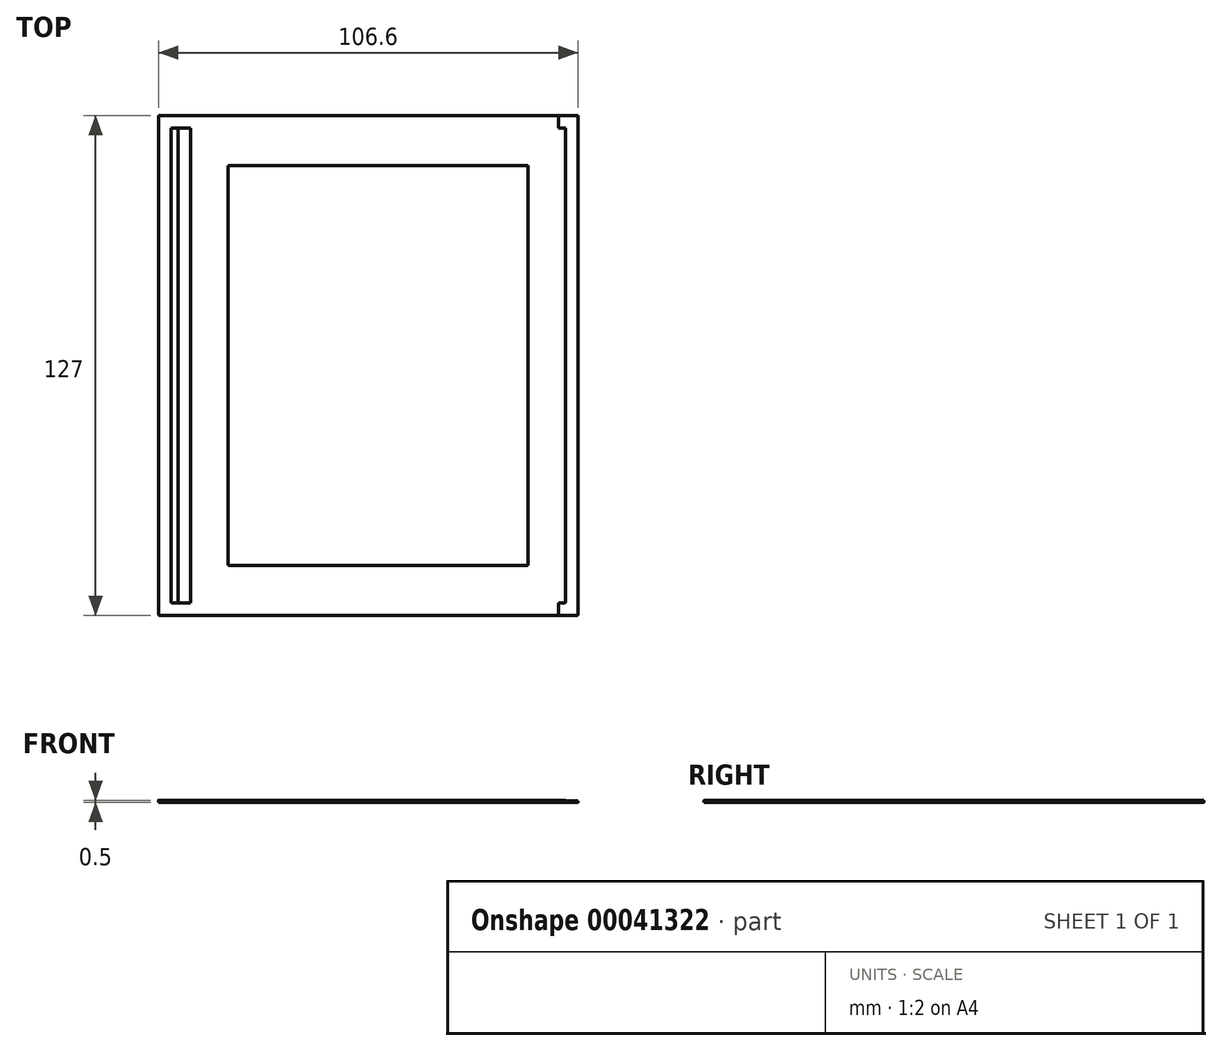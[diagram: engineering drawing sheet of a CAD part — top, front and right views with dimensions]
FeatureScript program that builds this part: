
annotation { "Feature Type Name" : "Feature", "Feature Type Description" : "" }
export const myFeature = defineFeature(function(context is Context, id is Id, definition is map)
    precondition{}
    {
        {
            assignVariable(context, id + "F0", {"name" : "Width", "anyValue" : 4});
        }
        {
            assignVariable(context, id + "F1", {"name" : "MaterialThickness", "anyValue" : .5});
        }
        {
            var Q0;
            Q0=qCreatedBy(makeId("Top.planeOp"),FACE);
            var sketch = newSketch(context, id + "F2", { "sketchPlane" : qUnion([Q0])});
            skLineSegment(sketch, "E0.rect.bottom", {"start": v(50.8, 63.5) * mm, "end": v(-50.8, 63.5) * mm});
            skLineSegment(sketch, "E0.rect.top", {"start": v(50.8, -63.5) * mm, "end": v(-50.8, -63.5) * mm});
            skLineSegment(sketch, "E0.rect.left", {"start": v(50.8, 63.5) * mm, "end": v(50.8, -63.5) * mm});
            skLineSegment(sketch, "E0.rect.right", {"start": v(-50.8, 63.5) * mm, "end": v(-50.8, -63.5) * mm});
            skPoint(sketch, "E0.rect.middle", {"position": v(0, 0) * mm});
            skLineSegment(sketch, "E1.0", {"start": v(38.1, 50.8) * mm, "end": v(-38.1, 50.8) * mm});
            skLineSegment(sketch, "E1.1", {"start": v(38.1, 50.8) * mm, "end": v(38.1, -50.8) * mm});
            skLineSegment(sketch, "E1.2", {"start": v(38.1, -50.8) * mm, "end": v(-38.1, -50.8) * mm});
            skLineSegment(sketch, "E1.3", {"start": v(-38.1, 50.8) * mm, "end": v(-38.1, -50.8) * mm});
            skLineSegment(sketch, "E2.0", {"start": v(47.63, 60.33) * mm, "end": v(-47.62, 60.33) * mm});
            skLineSegment(sketch, "E2.1", {"start": v(47.63, 60.33) * mm, "end": v(47.63, -60.33) * mm});
            skLineSegment(sketch, "E2.2", {"start": v(47.63, -60.33) * mm, "end": v(-47.63, -60.33) * mm});
            skLineSegment(sketch, "E2.3", {"start": v(-47.62, 60.32) * mm, "end": v(-47.63, -60.33) * mm});
            skSolve(sketch);
        }
        {
            var Q0;
            Q0=makeQuery(id+"F2.imprint","IMPRINT",FACE,{"disambiguationData":[TD([[makeQuery(id+"F2.imprint","IMPRINT",EDGE,{"derivedFrom":sQuery(id+"F2.wireOp",EDGE,"E0.rect.bottom")}),1.0]])]});
            extrude(context, id + "F3", {"entities" : qUnion([Q0]), "depth" : (getVariable(context, 'MaterialThickness') * (3 / 4)) * mm});
        }
        {
            var Q0;
            Q0=makeQuery(id+"F2.imprint","IMPRINT",FACE,{"disambiguationData":[TD([[makeQuery(id+"F2.imprint","IMPRINT",EDGE,{"derivedFrom":sQuery(id+"F2.wireOp",EDGE,"E1.0")}),1.0]])]});
            extrude(context, id + "F4", {"entities" : qUnion([Q0]), "depth" : (getVariable(context, 'MaterialThickness') * (1 / 4)) * mm});
        }
        {
            var Q0;
            Q0=makeQuery(id+"F2.imprint","IMPRINT",FACE,{"disambiguationData":[TD([[makeQuery(id+"F2.imprint","IMPRINT",EDGE,{"derivedFrom":sQuery(id+"F2.wireOp",EDGE,"E1.0")}),-1.0]])]});
            extrude(context, id + "F5", {"entities" : qUnion([Q0]), "operationType" : NewBodyOperationType.ADD, "depth" : (getVariable(context, 'MaterialThickness')) * mm});
        }
        {
            var Q0;
            Q0=makeQuery(id+"F3.opExtrude","SWEPT_BODY",BODY,{"disambiguationData":[OSD([sQuery(id+"F2.wireOp",EDGE,"E0.rect.bottom"),sQuery(id+"F2.wireOp",EDGE,"E0.rect.top"),sQuery(id+"F2.wireOp",EDGE,"E0.rect.left"),sQuery(id+"F2.wireOp",EDGE,"E0.rect.right"),sQuery(id+"F2.wireOp",EDGE,"E2.0"),sQuery(id+"F2.wireOp",EDGE,"E2.1"),sQuery(id+"F2.wireOp",EDGE,"E2.2"),sQuery(id+"F2.wireOp",EDGE,"E2.3")])]});
            transform(context, id + "F6", {"entities" : qUnion([Q0]), "transformType" : TransformType.TRANSLATION_3D, "dx" : (getVariable(context, 'Width') + 1) * mm, "dy" : 0 * mm, "dz" : 0 * mm, "makeCopy" : false});
        }
        {
            var Q0;
            Q0=makeQuery(id+"F2.imprint","IMPRINT",FACE,{"disambiguationData":[TD([[makeQuery(id+"F2.imprint","IMPRINT",EDGE,{"derivedFrom":sQuery(id+"F2.wireOp",EDGE,"E1.0")}),1.0]])]});
            var Q1;
            Q1=makeQuery(id+"F2.imprint","IMPRINT",FACE,{"disambiguationData":[TD([[makeQuery(id+"F2.imprint","IMPRINT",EDGE,{"derivedFrom":sQuery(id+"F2.wireOp",EDGE,"E1.0")}),-1.0]])]});
            extrude(context, id + "F7", {"entities" : qUnion([Q0, Q1]), "depth" : (getVariable(context, 'MaterialThickness') * (1 / 3)) * mm});
        }
        {
            var Q0;
            Q0=makeQuery(id+"F2.imprint","IMPRINT",FACE,{"disambiguationData":[TD([[makeQuery(id+"F2.imprint","IMPRINT",EDGE,{"derivedFrom":sQuery(id+"F2.wireOp",EDGE,"E0.rect.bottom")}),1.0]])]});
            extrude(context, id + "F8", {"entities" : qUnion([Q0]), "operationType" : NewBodyOperationType.ADD, "depth" : (getVariable(context, 'MaterialThickness')) * mm});
        }
        {
            assignVariable(context, id + "F9", {"name" : "BitDiameter", "anyValue" : .25});
        }
        {
            var Q0;
            Q0=makeQuery(id+"F3.opExtrude","SWEPT_EDGE",EDGE,{"disambiguationData":[OSD([sQuery(id+"F2.wireOp",EDGE,"E0.rect.top"),sQuery(id+"F2.wireOp",EDGE,"E0.rect.left")])]});
            var Q1;
            Q1=makeQuery(id+"F5.opExtrude","SWEPT_EDGE",EDGE,{"disambiguationData":[OSD([sQuery(id+"F2.wireOp",EDGE,"E2.1"),sQuery(id+"F2.wireOp",EDGE,"E2.2")])]});
            var Q2;
            Q2=makeQuery(id+"F5.opExtrude","SWEPT_EDGE",EDGE,{"disambiguationData":[OSD([sQuery(id+"F2.wireOp",EDGE,"E1.1"),sQuery(id+"F2.wireOp",EDGE,"E1.2")])]});
            var Q3;
            Q3=makeQuery(id+"F3.opExtrude","SWEPT_EDGE",EDGE,{"disambiguationData":[OSD([sQuery(id+"F2.wireOp",EDGE,"E0.rect.top"),sQuery(id+"F2.wireOp",EDGE,"E0.rect.right")])]});
            var Q4;
            Q4=makeQuery(id+"F5.opExtrude","SWEPT_EDGE",EDGE,{"disambiguationData":[OSD([sQuery(id+"F2.wireOp",EDGE,"E2.2"),sQuery(id+"F2.wireOp",EDGE,"E2.3")])]});
            var Q5;
            Q5=makeQuery(id+"F5.opExtrude","SWEPT_EDGE",EDGE,{"disambiguationData":[OSD([sQuery(id+"F2.wireOp",EDGE,"E1.2"),sQuery(id+"F2.wireOp",EDGE,"E1.3")])]});
            var Q6;
            Q6=makeQuery(id+"F3.opExtrude","SWEPT_EDGE",EDGE,{"disambiguationData":[OSD([sQuery(id+"F2.wireOp",EDGE,"E0.rect.bottom"),sQuery(id+"F2.wireOp",EDGE,"E0.rect.right")])]});
            var Q7;
            Q7=makeQuery(id+"F5.opExtrude","SWEPT_EDGE",EDGE,{"disambiguationData":[OSD([sQuery(id+"F2.wireOp",EDGE,"E2.0"),sQuery(id+"F2.wireOp",EDGE,"E2.3")])]});
            var Q8;
            Q8=makeQuery(id+"F5.opExtrude","SWEPT_EDGE",EDGE,{"disambiguationData":[OSD([sQuery(id+"F2.wireOp",EDGE,"E1.0"),sQuery(id+"F2.wireOp",EDGE,"E1.3")])]});
            var Q9;
            Q9=makeQuery(id+"F3.opExtrude","SWEPT_EDGE",EDGE,{"disambiguationData":[OSD([sQuery(id+"F2.wireOp",EDGE,"E0.rect.bottom"),sQuery(id+"F2.wireOp",EDGE,"E0.rect.left")])]});
            var Q10;
            Q10=makeQuery(id+"F5.opExtrude","SWEPT_EDGE",EDGE,{"disambiguationData":[OSD([sQuery(id+"F2.wireOp",EDGE,"E2.0"),sQuery(id+"F2.wireOp",EDGE,"E2.1")])]});
            var Q11;
            Q11=makeQuery(id+"F5.opExtrude","SWEPT_EDGE",EDGE,{"disambiguationData":[OSD([sQuery(id+"F2.wireOp",EDGE,"E1.0"),sQuery(id+"F2.wireOp",EDGE,"E1.1")])]});
            var Q12;
            Q12=makeQuery(id+"F4.opExtrude","CAP_EDGE",EDGE,{"disambiguationData":[OSD([sQuery(id+"F2.wireOp",EDGE,"E1.0")])],"isStart":false});
            var Q13;
            Q13=makeQuery(id+"F4.opExtrude","CAP_EDGE",EDGE,{"disambiguationData":[OSD([sQuery(id+"F2.wireOp",EDGE,"E1.1")])],"isStart":false});
            var Q14;
            Q14=makeQuery(id+"F4.opExtrude","CAP_EDGE",EDGE,{"disambiguationData":[OSD([sQuery(id+"F2.wireOp",EDGE,"E1.3")])],"isStart":false});
            var Q15;
            Q15=makeQuery(id+"F4.opExtrude","CAP_EDGE",EDGE,{"disambiguationData":[OSD([sQuery(id+"F2.wireOp",EDGE,"E1.2")])],"isStart":false});
            fillet(context, id + "F10", {"entities" : qUnion([Q0, Q1, Q2, Q3, Q4, Q5, Q6, Q7, Q8, Q9, Q10, Q11, Q12, Q13, Q14, Q15]), "radius" : (getVariable(context, 'BitDiameter')) * mm, "tangentPropagation" : true, "allowEdgeOverflow" : false});
        }
        {
            var Q0;
            Q0=makeQuery(id+"F8.opExtrude","SWEPT_EDGE",EDGE,{"disambiguationData":[OSD([sQuery(id+"F2.wireOp",EDGE,"E0.rect.bottom"),sQuery(id+"F2.wireOp",EDGE,"E0.rect.left")])]});
            var Q1;
            Q1=makeQuery(id+"F8.opExtrude","SWEPT_EDGE",EDGE,{"disambiguationData":[OSD([sQuery(id+"F2.wireOp",EDGE,"E2.0"),sQuery(id+"F2.wireOp",EDGE,"E2.1")])]});
            var Q2;
            Q2=makeQuery(id+"F8.opExtrude","SWEPT_EDGE",EDGE,{"disambiguationData":[OSD([sQuery(id+"F2.wireOp",EDGE,"E0.rect.bottom"),sQuery(id+"F2.wireOp",EDGE,"E0.rect.right")])]});
            var Q3;
            Q3=makeQuery(id+"F8.opExtrude","SWEPT_EDGE",EDGE,{"disambiguationData":[OSD([sQuery(id+"F2.wireOp",EDGE,"E2.0"),sQuery(id+"F2.wireOp",EDGE,"E2.3")])]});
            var Q4;
            Q4=makeQuery(id+"F8.opExtrude","SWEPT_EDGE",EDGE,{"disambiguationData":[OSD([sQuery(id+"F2.wireOp",EDGE,"E0.rect.top"),sQuery(id+"F2.wireOp",EDGE,"E0.rect.right")])]});
            var Q5;
            Q5=makeQuery(id+"F8.opExtrude","SWEPT_EDGE",EDGE,{"disambiguationData":[OSD([sQuery(id+"F2.wireOp",EDGE,"E2.2"),sQuery(id+"F2.wireOp",EDGE,"E2.3")])]});
            var Q6;
            Q6=makeQuery(id+"F8.opExtrude","SWEPT_EDGE",EDGE,{"disambiguationData":[OSD([sQuery(id+"F2.wireOp",EDGE,"E2.1"),sQuery(id+"F2.wireOp",EDGE,"E2.2")])]});
            var Q7;
            Q7=makeQuery(id+"F8.opExtrude","SWEPT_EDGE",EDGE,{"disambiguationData":[OSD([sQuery(id+"F2.wireOp",EDGE,"E0.rect.top"),sQuery(id+"F2.wireOp",EDGE,"E0.rect.left")])]});
            fillet(context, id + "F11", {"entities" : qUnion([Q0, Q1, Q2, Q3, Q4, Q5, Q6, Q7]), "radius" : (getVariable(context, 'BitDiameter')) * mm, "tangentPropagation" : true, "allowEdgeOverflow" : false});
        }
    });
